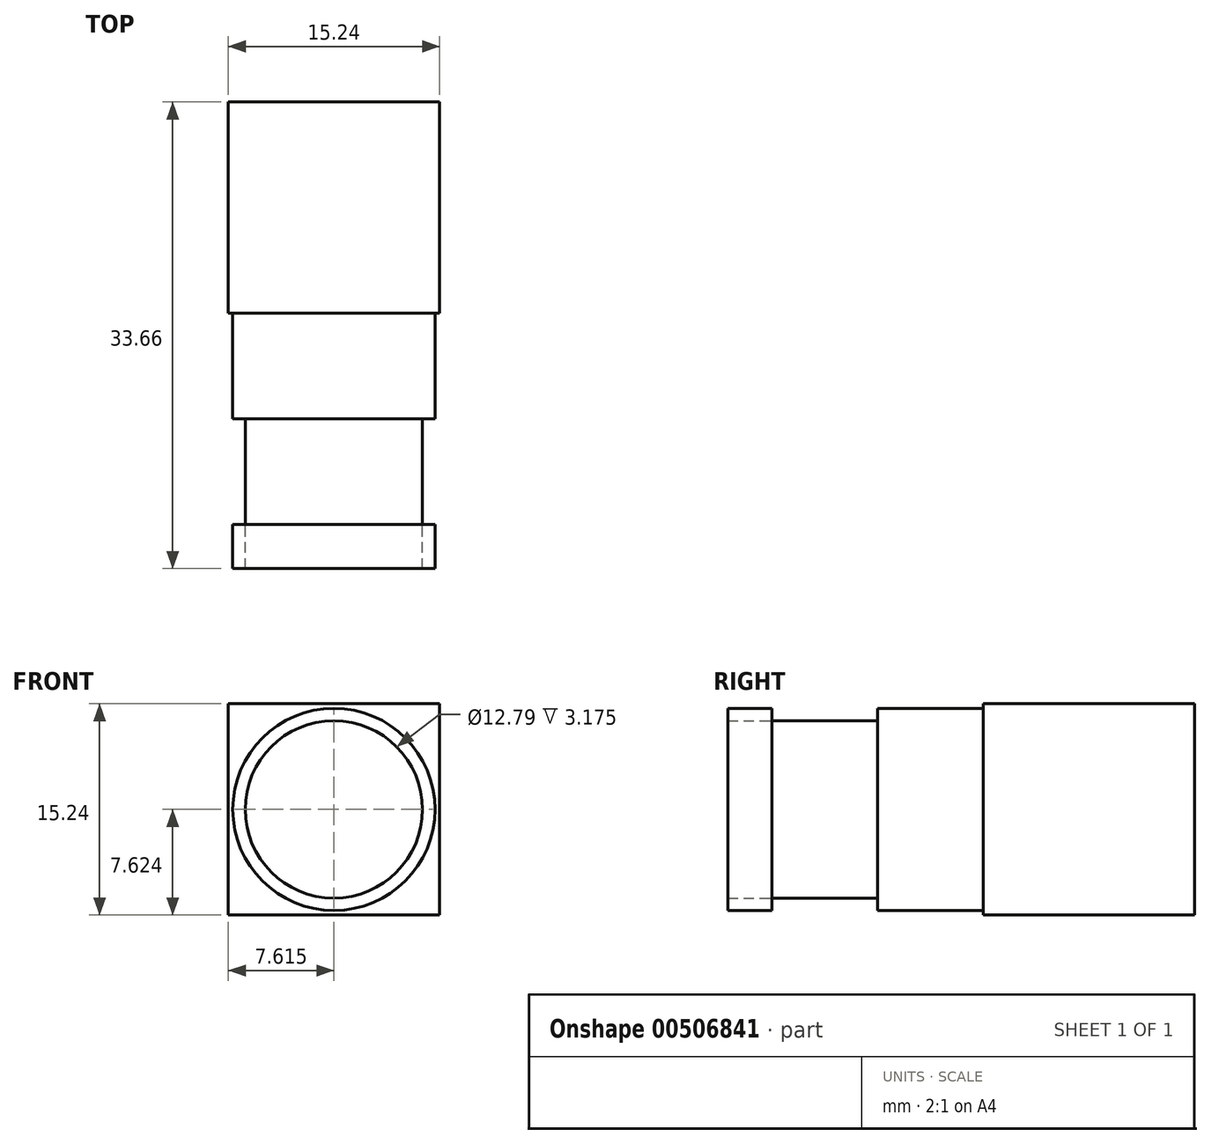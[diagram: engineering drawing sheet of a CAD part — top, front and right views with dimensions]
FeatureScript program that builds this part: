
annotation { "Feature Type Name" : "Feature", "Feature Type Description" : "" }
export const myFeature = defineFeature(function(context is Context, id is Id, definition is map)
    precondition{}
    {
        {
            var Q0;
            Q0=qCreatedBy(makeId("Front.planeOp"),FACE);
            var sketch = newSketch(context, id + "F0", { "sketchPlane" : qUnion([Q0])});
            skLineSegment(sketch, "E0.bottom", {"start": v(-52.78, 33.08) * mm, "end": v(-37.54, 33.08) * mm});
            skLineSegment(sketch, "E0.top", {"start": v(-52.78, 17.84) * mm, "end": v(-37.54, 17.84) * mm});
            skLineSegment(sketch, "E0.left", {"start": v(-52.78, 33.08) * mm, "end": v(-52.78, 17.84) * mm});
            skLineSegment(sketch, "E0.right", {"start": v(-37.54, 33.08) * mm, "end": v(-37.54, 17.84) * mm});
            skSolve(sketch);
        }
        {
            var Q0;
            Q0=makeQuery(id+"F0.imprint","IMPRINT",FACE,{"disambiguationData":[TD([[makeQuery(id+"F0.imprint","IMPRINT",EDGE,{"derivedFrom":sQuery(id+"F0.wireOp",EDGE,"E0.bottom")}),-1.0]])]});
            extrude(context, id + "F1", {"entities" : qUnion([Q0]), "depth" : 15.24 * mm, "offsetDistance" : 25.4 * mm});
        }
        {
            var Q0;
            Q0=makeQuery(id+"F1.opExtrude","CAP_FACE",FACE,{"disambiguationData":[OSD([sQuery(id+"F0.wireOp",EDGE,"E0.bottom"),sQuery(id+"F0.wireOp",EDGE,"E0.top"),sQuery(id+"F0.wireOp",EDGE,"E0.left"),sQuery(id+"F0.wireOp",EDGE,"E0.right")])],"isStart":false});
            var sketch = newSketch(context, id + "F2", { "sketchPlane" : qUnion([Q0])});
            skCircle(sketch, "E1", {"center": v(-45.16, 25.46) * mm, "radius": 7.3 * mm});
            skPoint(sketch, "E1.centerSnap0", {"position": v(-45.16, 17.84) * mm});
            skPoint(sketch, "E1.centerSnap1", {"position": v(-52.78, 25.46) * mm});
            skSolve(sketch);
        }
        {
            var Q0;
            Q0=makeQuery(id+"F2.imprint","IMPRINT",FACE,{"disambiguationData":[TD([[makeQuery(id+"F2.imprint","IMPRINT",EDGE,{"derivedFrom":sQuery(id+"F2.wireOp",EDGE,"E1")}),1.0]])]});
            extrude(context, id + "F3", {"entities" : qUnion([Q0]), "operationType" : NewBodyOperationType.ADD, "depth" : 7.62 * mm, "offsetDistance" : 25.4 * mm});
        }
        {
            var Q0;
            Q0=makeQuery(id+"F3.opExtrude","CAP_FACE",FACE,{"disambiguationData":[OSD([sQuery(id+"F2.wireOp",EDGE,"E1")])],"isStart":false});
            var sketch = newSketch(context, id + "F4", { "sketchPlane" : qUnion([Q0])});
            skCircle(sketch, "E2", {"center": v(-45.16, 25.46) * mm, "radius": 6.4 * mm});
            skSolve(sketch);
        }
        {
            var Q0;
            Q0=makeQuery(id+"F4.imprint","IMPRINT",FACE,{"disambiguationData":[TD([[makeQuery(id+"F4.imprint","IMPRINT",EDGE,{"derivedFrom":sQuery(id+"F4.wireOp",EDGE,"E2")}),1.0]])]});
            extrude(context, id + "F5", {"entities" : qUnion([Q0]), "operationType" : NewBodyOperationType.ADD, "depth" : 7.62 * mm, "offsetDistance" : 25.4 * mm});
        }
        {
            var Q0;
            Q0=makeQuery(id+"F5.opExtrude","CAP_FACE",FACE,{"disambiguationData":[OSD([sQuery(id+"F4.wireOp",EDGE,"E2")])],"isStart":false});
            var sketch = newSketch(context, id + "F6", { "sketchPlane" : qUnion([Q0])});
            skCircle(sketch, "E3", {"center": v(-45.16, 25.46) * mm, "radius": 7.3 * mm});
            skSolve(sketch);
        }
        {
            var Q0;
            Q0=makeQuery(id+"F6.imprint","IMPRINT",FACE,{"disambiguationData":[TD([[makeQuery(id+"F6.imprint","IMPRINT",EDGE,{"derivedFrom":sQuery(id+"F6.wireOp",EDGE,"E3")}),1.0]])]});
            extrude(context, id + "F7", {"entities" : qUnion([Q0]), "depth" : 3.17 * mm, "offsetDistance" : 25.4 * mm});
        }
    });
